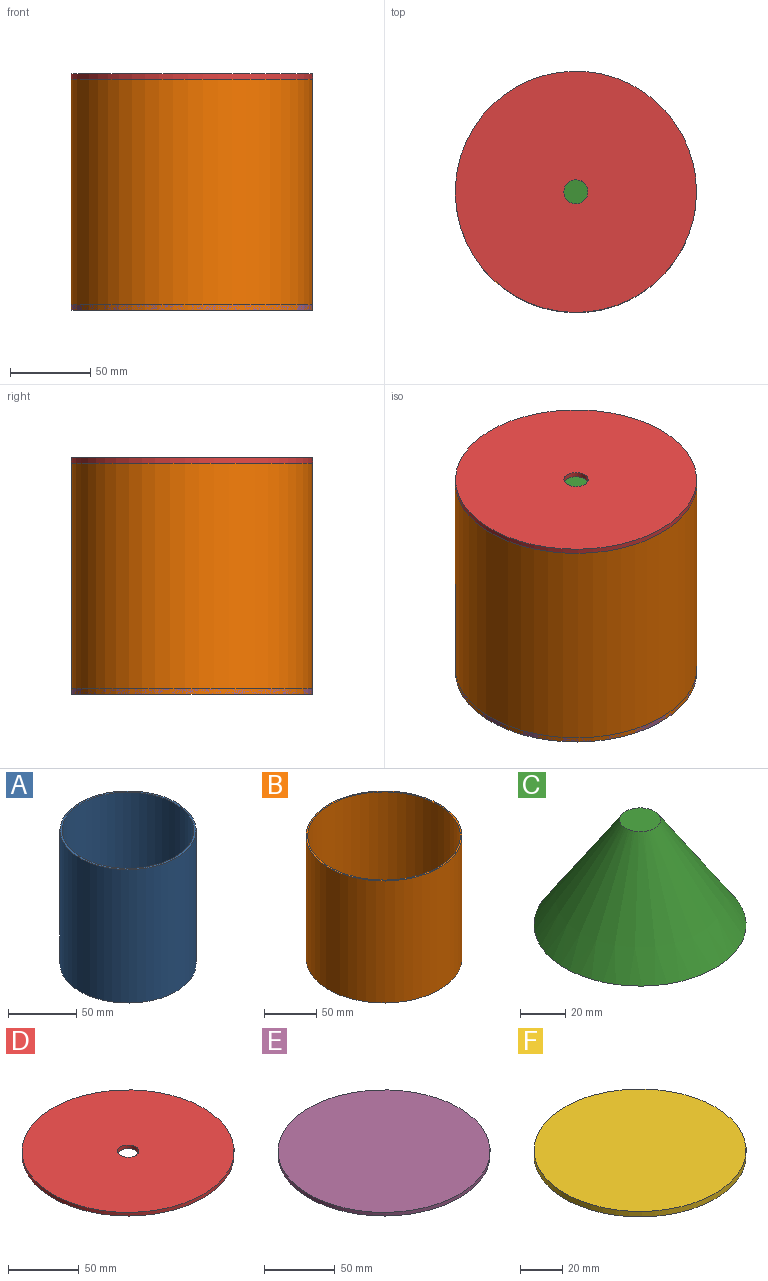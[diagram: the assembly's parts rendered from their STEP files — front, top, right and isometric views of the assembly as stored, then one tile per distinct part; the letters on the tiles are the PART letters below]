
ASSEMBLY  parts=6 mates=5
PART A: 4 faces, bbox 100x100x120 mm
  f0: cylinder r=48.41mm len=120mm, axis (0,0,-1), area 36502.2mm2, adj f2,f3
  f1: cylinder r=50mm len=120mm, axis (0,0,-1), area 37699.1mm2, adj f2,f3
  f2: plane 100x100mm, normal (0,0,1), area 490.8mm2, adj f0,f1
  f3: plane 100x100mm, normal (0,0,-1), area 490.8mm2, adj f0,f1
PART B: 4 faces, bbox 150x150x143.7 mm
  f0: cylinder r=73.41mm len=146.83mm, axis (0,0,-1), area 66260.6mm2, adj f2,f3
  f1: cylinder r=75mm len=150mm, axis (0,0,-1), area 67693.5mm2, adj f2,f3
  f2: plane 150x150mm, normal (0,0,1), area 740.2mm2, adj f0,f1
  f3: plane 150x150mm, normal (0,0,-1), area 740.2mm2, adj f0,f1
PART C: 3 faces, bbox 93.7x93.7x56.8 mm
  f0: plane 93.65x93.65mm, normal (0,0,-1), area 6888.2mm2, adj f2
  f1: plane 18.18x18.18mm, normal (0,0,1), area 259.4mm2, adj f2
  f2: cone r=46.82mm half-angle=33.6deg, axis (0,0,-1), area 11982.1mm2, adj f0,f1
PART D: 4 faces, bbox 150x150x3.2 mm
  f0: cylinder r=7.5mm len=15mm, axis (0,0,-1), area 149.6mm2, adj f2,f3
  f1: cylinder r=75mm len=150mm, axis (0,0,-1), area 1496.2mm2, adj f2,f3
  f2: plane 150x150mm, normal (0,0,1), area 17494.7mm2, adj f0,f1
  f3: plane 150x150mm, normal (0,0,-1), area 17494.7mm2, adj f0,f1
PART E: 3 faces, bbox 150x150x3.2 mm
  f0: cylinder r=75mm len=150mm, axis (0,0,-1), area 1496.2mm2, adj f1,f2
  f1: plane 150x150mm, normal (0,0,1), area 17671.5mm2, adj f0
  f2: plane 150x150mm, normal (0,0,-1), area 17671.5mm2, adj f0
PART F: 3 faces, bbox 100x100x3.2 mm
  f0: cylinder r=50mm len=100mm, axis (0,0,-1), area 997.5mm2, adj f1,f2
  f1: plane 100x100mm, normal (0,0,1), area 7854mm2, adj f0
  f2: plane 100x100mm, normal (0,0,-1), area 7854mm2, adj f0
PLACE A t=(24.7,55.01,27.41)mm
PLACE B t=(24.7,55.01,3.76)mm
PLACE C rot(axis=(0,1,0),180deg) t=(24.7,55.01,150.59)mm
PLACE D t=(24.7,55.01,147.41)mm
PLACE E t=(24.7,55.01,3.76)mm
PLACE F t=(24.7,55.01,24.24)mm
MATE fastened A.f0 <-> B.f0  axis (0,0,1) through (24.7,55.01,147.41)mm
MATE fastened A.f0 <-> F.f0  axis (0,0,-1) through (24.7,55.01,27.41)mm
MATE fastened B.f0 <-> E.f0  axis (0,0,-1) through (24.7,55.01,3.76)mm
MATE fastened D.f1 <-> B.f0  axis (0,0,-1) through (24.7,55.01,147.41)mm
MATE fastened C.f2 <-> D.f1  axis (0,0,1) through (24.7,55.01,147.41)mm
